# Revit family: HL_Дворовый трап серии Perfekt_HL616.1H
name_source: partatom
category: Instalační zařizovací předměty
revit_build: Autodesk Revit 2016 (Build: 20161004_0715(x64)
units: mm (PartAtom-declared; Revit-internal decimal feet)

## family parameters
Bod výpočtu místnosti = Ano
Kóta kulaté spojky = Použít průměr
Nadpis OmniClass = Deck Waste Water Drains
Ořezat dutým tvarem při načtení = Ne
Sdílené = Ne
Typ součásti = Normální
Vždy vertikální = Ano
Založené na pracovní rovině = Ne
Číslo OmniClass = 23.70.50.21.24.14

## types (2) — shared parameters
Připojení CW = Ne
Připojení HW = Ne
Připojení odpadu = Ano
Připojení ventilace = Ne
URL = http://www.hutterer-lechner.com
Výrobce = HL Hutterer & Lechner GmbH
ВЫСОТА МОНТАЖА = 252 mm
МАКСИМАЛЬНАЯ НАГРУЗКА КЛАССА = B - 12,5 t (außen)
МАТЕРИАЛ = PP
НАСАДКА = 55-135 mm/260 x 260 mm Guss
РЕШЁТКА = Gusseisen 226 x 226 mm

## per-type parameters (varying)
| type | EAN | Klíčová poznámka | Komentáře k typům | Model | Popis | ВЕС | НОМИНАЛЬНЫЙ ДИАМЕТР | ПРОИЗВОДИТЕЛЬНОСТЬ | РАЗМЕР |
| HL_Дворовый трап серии Perfekt_HL616.1H_1 | 9003076962617 | HL616.1H/1 | Дворовый трап серии Perfekt DN110 вертикальный с битумным полотном, 260х260мм/226х226мм чугун с морозоустойчивой запахозапирающей заслонкой. | HL616.1H/1 | Дворовый трап серии Perfekt DN110 вертикальный | 13,523 kg | 110 mm | 5,5 l/s | DN110 |
| HL_Дворовый трап серии Perfekt_HL616.1H_5 | 9003076951611 | HL616.1H/5 | Дворовый трап серии Perfekt DN160 вертикальный с битумным полотном, 260х260мм/226х226мм чугун с морозоустойчивой запахозапирающей заслонкой. | HL616.1H/5 | Дворовый трап серии Perfekt DN160 вертикальный | 13,53 kg | 160 mm | 4,8 l/s | DN160 |

## geometry (parser evidence)
native form markers: Sweep x3
no freeform markers — native parametric forms only
